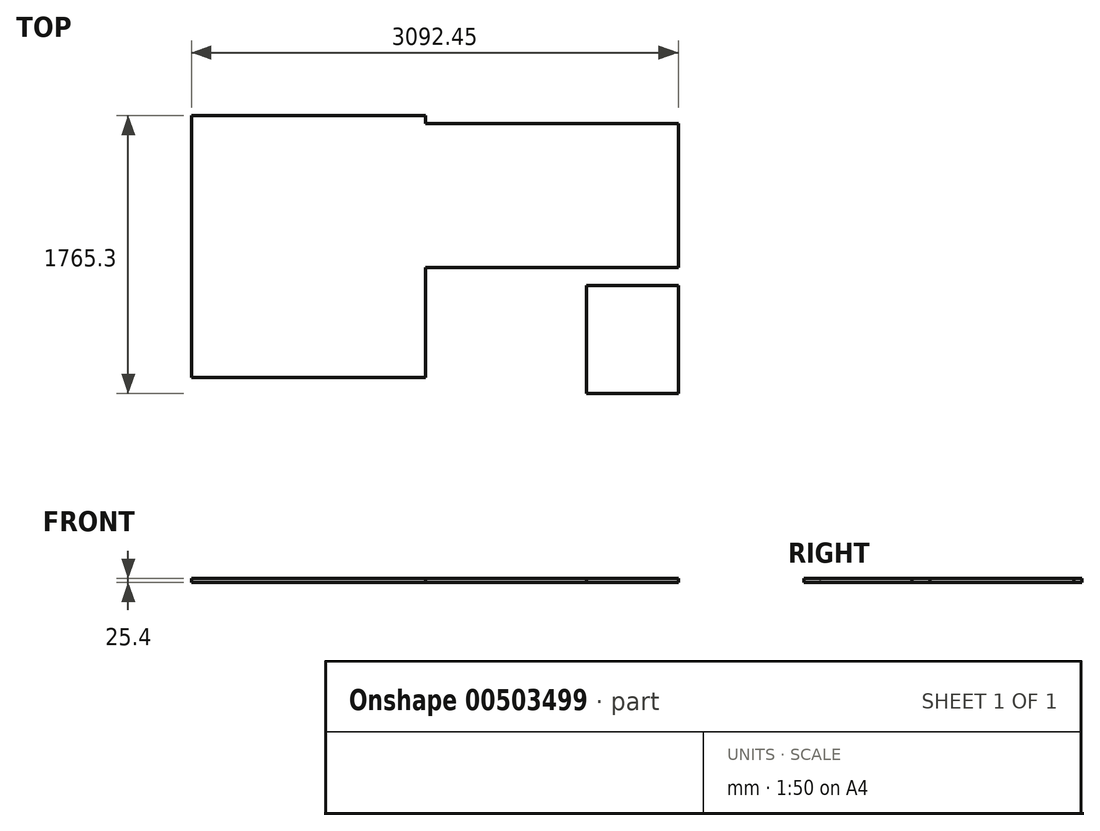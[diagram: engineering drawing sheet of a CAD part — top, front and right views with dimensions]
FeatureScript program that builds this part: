
annotation { "Feature Type Name" : "Feature", "Feature Type Description" : "" }
export const myFeature = defineFeature(function(context is Context, id is Id, definition is map)
    precondition{}
    {
        {
            var Q0;
            Q0=qCreatedBy(makeId("Top.planeOp"),FACE);
            var sketch = newSketch(context, id + "F0", { "sketchPlane" : qUnion([Q0])});
            skLineSegment(sketch, "E0.bottom", {"start": v(0, 0) * mm, "end": v(1485.9, 0) * mm});
            skLineSegment(sketch, "E0.top", {"start": v(0, -1663.7) * mm, "end": v(1485.9, -1663.7) * mm});
            skLineSegment(sketch, "E0.left", {"start": v(0, 0) * mm, "end": v(0, -1663.7) * mm});
            skLineSegment(sketch, "E0.right", {"start": v(1485.9, 0) * mm, "end": v(1485.9, -1663.7) * mm});
            skLineSegment(sketch, "E1.bottom", {"start": v(1485.9, -50.8) * mm, "end": v(3092.45, -50.8) * mm});
            skLineSegment(sketch, "E1.top", {"start": v(1485.9, -965.2) * mm, "end": v(3092.45, -965.2) * mm});
            skLineSegment(sketch, "E1.left", {"start": v(1485.9, -50.8) * mm, "end": v(1485.9, -965.2) * mm});
            skLineSegment(sketch, "E1.right", {"start": v(3092.45, -50.8) * mm, "end": v(3092.45, -965.2) * mm});
            skLineSegment(sketch, "E2.bottom", {"start": v(2559.05, -965.2) * mm, "end": v(2978.15, -965.2) * mm});
            skLineSegment(sketch, "E2.top", {"start": v(2559.05, -1079.5) * mm, "end": v(2978.15, -1079.5) * mm});
            skLineSegment(sketch, "E2.left", {"start": v(2559.05, -965.2) * mm, "end": v(2559.05, -1079.5) * mm});
            skLineSegment(sketch, "E2.right", {"start": v(2978.15, -965.2) * mm, "end": v(2978.15, -1079.5) * mm});
            skLineSegment(sketch, "E3.bottom", {"start": v(2508.25, -1079.5) * mm, "end": v(3092.45, -1079.5) * mm});
            skLineSegment(sketch, "E3.top", {"start": v(2508.25, -1765.3) * mm, "end": v(3092.45, -1765.3) * mm});
            skLineSegment(sketch, "E3.left", {"start": v(2508.25, -1079.5) * mm, "end": v(2508.25, -1765.3) * mm});
            skLineSegment(sketch, "E3.right", {"start": v(3092.45, -1079.5) * mm, "end": v(3092.45, -1765.3) * mm});
            skLineSegment(sketch, "E4.bottom", {"start": v(1485.9, -965.2) * mm, "end": v(2381.25, -965.2) * mm});
            skLineSegment(sketch, "E4.top", {"start": v(1485.9, -1663.7) * mm, "end": v(2381.25, -1663.7) * mm});
            skLineSegment(sketch, "E4.left", {"start": v(1485.9, -965.2) * mm, "end": v(1485.9, -1663.7) * mm});
            skLineSegment(sketch, "E4.right", {"start": v(2381.25, -965.2) * mm, "end": v(2381.25, -1663.7) * mm});
            skSolve(sketch);
        }
        {
            var Q0;
            Q0=makeQuery(id+"F0.imprint","IMPRINT",FACE,{"disambiguationData":[TD([[makeQuery(id+"F0.imprint","IMPRINT",EDGE,{"derivedFrom":sQuery(id+"F0.wireOp",EDGE,"E0.bottom")}),-1.0]])]});
            var Q1;
            Q1=makeQuery(id+"F0.imprint","IMPRINT",FACE,{"disambiguationData":[TD([[makeQuery(id+"F0.imprint","IMPRINT",EDGE,{"derivedFrom":sQuery(id+"F0.wireOp",EDGE,"E1.bottom")}),-1.0]])]});
            var Q2;
            Q2=makeQuery(id+"F0.imprint","IMPRINT",FACE,{"disambiguationData":[TD([[makeQuery(id+"F0.imprint","IMPRINT",EDGE,{"derivedFrom":sQuery(id+"F0.wireOp",EDGE,"E4.bottom")}),-1.0]])]});
            var Q3;
            Q3=makeQuery(id+"F0.imprint","IMPRINT",FACE,{"disambiguationData":[TD([[makeQuery(id+"F0.imprint","IMPRINT",EDGE,{"derivedFrom":sQuery(id+"F0.wireOp",EDGE,"E3.top")}),1.0]])]});
            var Q4;
            Q4=makeQuery(id+"F0.imprint","IMPRINT",FACE,{"disambiguationData":[TD([[makeQuery(id+"F0.imprint","IMPRINT",EDGE,{"derivedFrom":sQuery(id+"F0.wireOp",EDGE,"E2.bottom")}),-1.0]])]});
            extrude(context, id + "F1", {"entities" : qUnion([Q0, Q1, Q2, Q3, Q4]), "depth" : 25.4 * mm});
        }
    });
